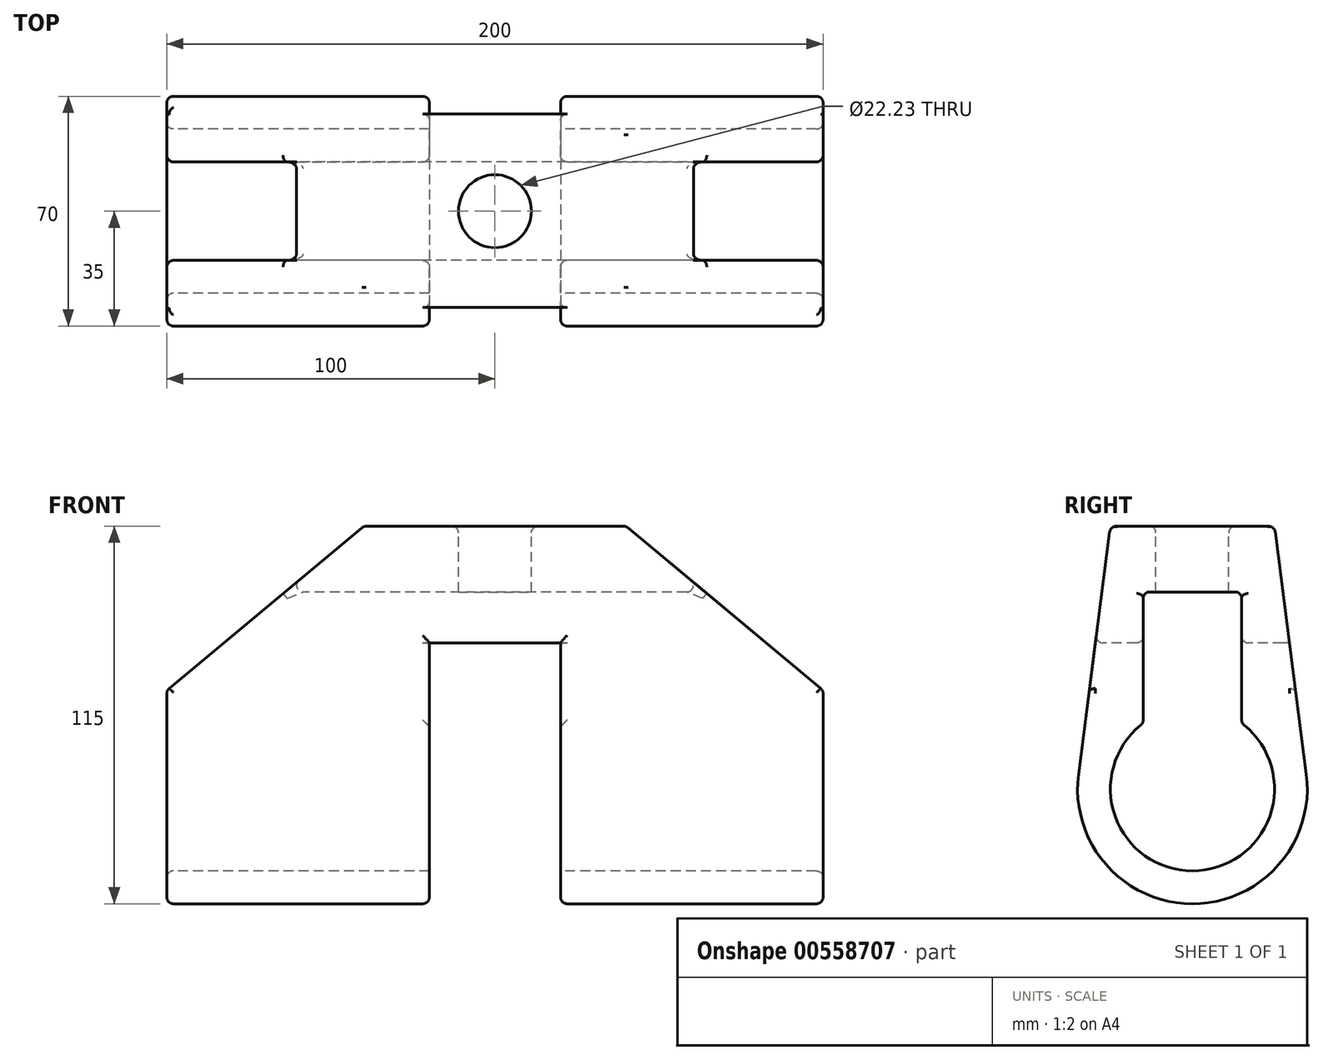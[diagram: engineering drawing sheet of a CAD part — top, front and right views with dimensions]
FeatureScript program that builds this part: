
annotation { "Feature Type Name" : "Feature", "Feature Type Description" : "" }
export const myFeature = defineFeature(function(context is Context, id is Id, definition is map)
    precondition{}
    {
        {
            var Q0;
            Q0=qCreatedBy(makeId("Right.planeOp"),FACE);
            var sketch = newSketch(context, id + "F0", { "sketchPlane" : qUnion([Q0])});
            skLineSegment(sketch, "E0", {"start": v(0, 89.77) * mm, "end": v(0, -61.35) * mm, "construction": true});
            skLineSegment(sketch, "E1", {"start": v(0, 80) * mm, "end": v(25, 80) * mm});
            skCircle(sketch, "E2", {"center": v(0, 0) * mm, "radius": 35 * mm});
            skLineSegment(sketch, "E3", {"start": v(25, 80) * mm, "end": v(34.71, 4.46) * mm});
            skLineSegment(sketch, "E4.MirrorCS", {"start": v(0, 80) * mm, "end": v(-25, 80) * mm});
            skLineSegment(sketch, "E5.MirrorCS", {"start": v(-25, 80) * mm, "end": v(-34.71, 4.46) * mm});
            skCircle(sketch, "E6", {"center": v(0, 0) * mm, "radius": 25 * mm});
            skLineSegment(sketch, "E7", {"start": v(0, 60) * mm, "end": v(-15, 60) * mm});
            skLineSegment(sketch, "E8", {"start": v(-15, 60) * mm, "end": v(-15, 20) * mm});
            skLineSegment(sketch, "E9.MirrorCS", {"start": v(0, 60) * mm, "end": v(15, 60) * mm});
            skLineSegment(sketch, "E10.MirrorCS", {"start": v(15, 60) * mm, "end": v(15, 20) * mm});
            skSolve(sketch);
        }
        {
            var Q0;
            Q0=makeQuery(id+"F0.imprint","IMPRINT",FACE,{"disambiguationData":[TD([[makeQuery(id+"F0.imprint","IMPRINT",EDGE,{"derivedFrom":sQuery(id+"F0.wireOp",EDGE,"E1")}),-1.0]])]});
            var Q1;
            {var subQ5=sQuery(id+"F0.wireOp",EDGE,"E2");var subQ6=makeQuery(id+"F0.imprint","INTERSECT",VERTEX,{"derivedFrom":[subQ5,sQuery(id+"F0.wireOp",EDGE,"E3")]});Q1=makeQuery(id+"F0.imprint","IMPRINT",FACE,{"disambiguationData":[TD([[makeQuery(id+"F0.imprint","IMPRINT",EDGE,{"disambiguationData":[TD([[subQ6,-1.0]])],"derivedFrom":subQ5}),1.0]])]});}
            extrude(context, id + "F1", {"entities" : qUnion([Q0, Q1]), "endBound" : BoundingType.SYMMETRIC, "depth" : 200 * mm, "offsetDistance" : 25 * mm});
        }
        {
            var Q0;
            Q0=qCreatedBy(makeId("Front.planeOp"),FACE);
            var sketch = newSketch(context, id + "F2", { "sketchPlane" : qUnion([Q0])});
            skLineSegment(sketch, "E11", {"start": v(0, 98.43) * mm, "end": v(0, -84.02) * mm, "construction": true});
            skLineSegment(sketch, "E12", {"start": v(-100, 60) * mm, "end": v(-100, 80) * mm});
            skLineSegment(sketch, "E13", {"start": v(-100, -35) * mm, "end": v(-100, -25) * mm});
            skLineSegment(sketch, "E14", {"start": v(100, 80) * mm, "end": v(-100, 80) * mm});
            skLineSegment(sketch, "E15", {"start": v(-100, 60) * mm, "end": v(-100, -25) * mm});
            skLineSegment(sketch, "E16", {"start": v(-40, 80) * mm, "end": v(-100, 30) * mm});
            skLineSegment(sketch, "E17.MirrorCS", {"start": v(100, 60) * mm, "end": v(100, 80) * mm});
            skLineSegment(sketch, "E18.MirrorCS", {"start": v(100, 60) * mm, "end": v(100, -25) * mm});
            skLineSegment(sketch, "E19.MirrorCS", {"start": v(40, 80) * mm, "end": v(100, 30) * mm});
            skLineSegment(sketch, "E20", {"start": v(100, -35) * mm, "end": v(-100, -35) * mm});
            skLineSegment(sketch, "E21", {"start": v(0, 44.46) * mm, "end": v(20, 44.46) * mm});
            skLineSegment(sketch, "E22", {"start": v(20, 44.46) * mm, "end": v(20, -35) * mm});
            skLineSegment(sketch, "E23.MirrorCS", {"start": v(0, 44.46) * mm, "end": v(-20, 44.46) * mm});
            skLineSegment(sketch, "E24.MirrorCS", {"start": v(-20, 44.46) * mm, "end": v(-20, -35) * mm});
            skSolve(sketch);
        }
        {
            var Q0;
            Q0 = qSketchRegion(id + "F2", true);
            extrude(context, id + "F3", {"entities" : qUnion([Q0]), "operationType" : NewBodyOperationType.REMOVE, "endBound" : BoundingType.SYMMETRIC, "oppositeDirection" : true, "depth" : 300 * mm, "offsetDistance" : 25 * mm});
        }
        {
            var Q0;
            Q0=makeQuery(id+"F1.opExtrude","SWEPT_FACE",FACE,{"disambiguationData":[OSD([sQuery(id+"F0.wireOp",EDGE,"E1"),sQuery(id+"F0.wireOp",EDGE,"E4.MirrorCS")])]});
            var sketch = newSketch(context, id + "F4", { "sketchPlane" : qUnion([Q0])});
            skPoint(sketch, "E25", {"position": v(0, 0) * mm});
            skSolve(sketch);
        }
        {
            var Q0;
            Q0=sQuery(id+"F4.wireOp",VERTEX,"E25");
            var Q1;
            Q1=makeQuery(id+"F1.opExtrude","SWEPT_BODY",BODY,{"disambiguationData":[OSD([sQuery(id+"F0.wireOp",EDGE,"E1"),sQuery(id+"F0.wireOp",EDGE,"E2"),sQuery(id+"F0.wireOp",EDGE,"E3"),sQuery(id+"F0.wireOp",EDGE,"E4.MirrorCS"),sQuery(id+"F0.wireOp",EDGE,"E5.MirrorCS"),sQuery(id+"F0.wireOp",EDGE,"E6")])]});
            hole(context, id + "F5", {"style" : HoleStyle.SIMPLE, "endStyle" : HoleEndStyle.THROUGH, "standardTappedOrClearance" : lookupTablePath({ "standard" : "ANSI", "engagement" : "75%", "pitch" : "8 tpi", "size" : "1", "type" : "Tapped" }), "standardBlindInLast" : lookupTablePath({ "standard" : "ANSI", "engagement" : "75%", "pitch" : "8 tpi", "size" : "1", "type" : "Tapped" }), "holeDiameter" : 22.22 * mm, "majorDiameter" : 25.4 * mm, "showTappedDepth" : true, "isTappedThrough" : true, "tappedDepth" : 3.6 * mm, "tapClearance" : 3, "locations" : qUnion([Q0]), "scope" : qUnion([Q1])});
        }
        {
            var Q0;
            Q0=makeQuery(id+"F1.opExtrude","SWEPT_FACE",FACE,{"disambiguationData":[OSD([sQuery(id+"F0.wireOp",EDGE,"E1"),sQuery(id+"F0.wireOp",EDGE,"E4.MirrorCS")])]});
            var Q1;
            Q1=makeQuery(id+"F1.opExtrude","SWEPT_FACE",FACE,{"disambiguationData":[OSD([sQuery(id+"F0.wireOp",EDGE,"E5.MirrorCS")])]});
            var Q2;
            Q2=makeQuery(id+"F3.boolean.opBoolean","COPY",FACE,{"derivedFrom":makeQuery(id+"F3.opExtrude","SWEPT_FACE",FACE,{"disambiguationData":[OSD([sQuery(id+"F2.wireOp",EDGE,"E16")])]})});
            var Q3;
            Q3=makeQuery(id+"F1.opExtrude","CAP_FACE",FACE,{"disambiguationData":[OSD([sQuery(id+"F0.wireOp",EDGE,"E1"),sQuery(id+"F0.wireOp",EDGE,"E2"),sQuery(id+"F0.wireOp",EDGE,"E3"),sQuery(id+"F0.wireOp",EDGE,"E4.MirrorCS"),sQuery(id+"F0.wireOp",EDGE,"E5.MirrorCS"),sQuery(id+"F0.wireOp",EDGE,"E6"),sQuery(id+"F0.wireOp",EDGE,"E7"),sQuery(id+"F0.wireOp",EDGE,"E8"),sQuery(id+"F0.wireOp",EDGE,"E9.MirrorCS"),sQuery(id+"F0.wireOp",EDGE,"E10.MirrorCS")])],"isStart":true});
            var Q4;
            Q4=makeQuery(id+"F3.boolean.opBoolean","COPY",FACE,{"derivedFrom":makeQuery(id+"F3.opExtrude","SWEPT_FACE",FACE,{"disambiguationData":[OSD([sQuery(id+"F2.wireOp",EDGE,"E19.MirrorCS")])]})});
            var Q5;
            Q5=makeQuery(id+"F1.opExtrude","CAP_FACE",FACE,{"disambiguationData":[OSD([sQuery(id+"F0.wireOp",EDGE,"E1"),sQuery(id+"F0.wireOp",EDGE,"E2"),sQuery(id+"F0.wireOp",EDGE,"E3"),sQuery(id+"F0.wireOp",EDGE,"E4.MirrorCS"),sQuery(id+"F0.wireOp",EDGE,"E5.MirrorCS"),sQuery(id+"F0.wireOp",EDGE,"E6"),sQuery(id+"F0.wireOp",EDGE,"E7"),sQuery(id+"F0.wireOp",EDGE,"E8"),sQuery(id+"F0.wireOp",EDGE,"E9.MirrorCS"),sQuery(id+"F0.wireOp",EDGE,"E10.MirrorCS")])],"isStart":false});
            var Q6;
            Q6=makeQuery(id+"F3.boolean.opBoolean","COPY",FACE,{"derivedFrom":makeQuery(id+"F3.opExtrude","SWEPT_FACE",FACE,{"disambiguationData":[OSD([sQuery(id+"F2.wireOp",EDGE,"XbkMvuSp-rH2C-ZSdh-ISZn-jGzENHmFmOjn.right")])]})});
            var Q7;
            Q7=makeQuery(id+"F3.boolean.opBoolean","COPY",FACE,{"derivedFrom":makeQuery(id+"F3.opExtrude","SWEPT_FACE",FACE,{"disambiguationData":[OSD([sQuery(id+"F2.wireOp",EDGE,"XbkMvuSp-rH2C-ZSdh-ISZn-jGzENHmFmOjn.left")])]})});
            var Q8;
            {var subQ2=sQuery(id+"F0.wireOp",EDGE,"E6");Q8=makeQuery(id+"F3.boolean.opBoolean","SPLIT",FACE,{"disambiguationData":[TD([makeQuery(id+"F3.opExtrude","SWEPT_FACE",FACE,{"disambiguationData":[OSD([sQuery(id+"F2.wireOp",EDGE,"XbkMvuSp-rH2C-ZSdh-ISZn-jGzENHmFmOjn.left")])]})])],"derivedFrom":makeQuery(id+"F1.opExtrude","SWEPT_FACE",FACE,{"disambiguationData":[OSD([subQ2])]})});}
            var Q9;
            Q9=makeQuery(id+"F1.opExtrude","SWEPT_FACE",FACE,{"disambiguationData":[OSD([sQuery(id+"F0.wireOp",EDGE,"E10.MirrorCS")])]});
            var Q10;
            Q10=makeQuery(id+"F1.opExtrude","SWEPT_FACE",FACE,{"disambiguationData":[OSD([sQuery(id+"F0.wireOp",EDGE,"E8")])]});
            fillet(context, id + "F6", {"entities" : qUnion([Q0, Q1, Q2, Q3, Q4, Q5, Q6, Q7, Q8, Q9, Q10]), "radius" : 2 * mm, "tangentPropagation" : true, "allowEdgeOverflow" : false});
        }
    });
